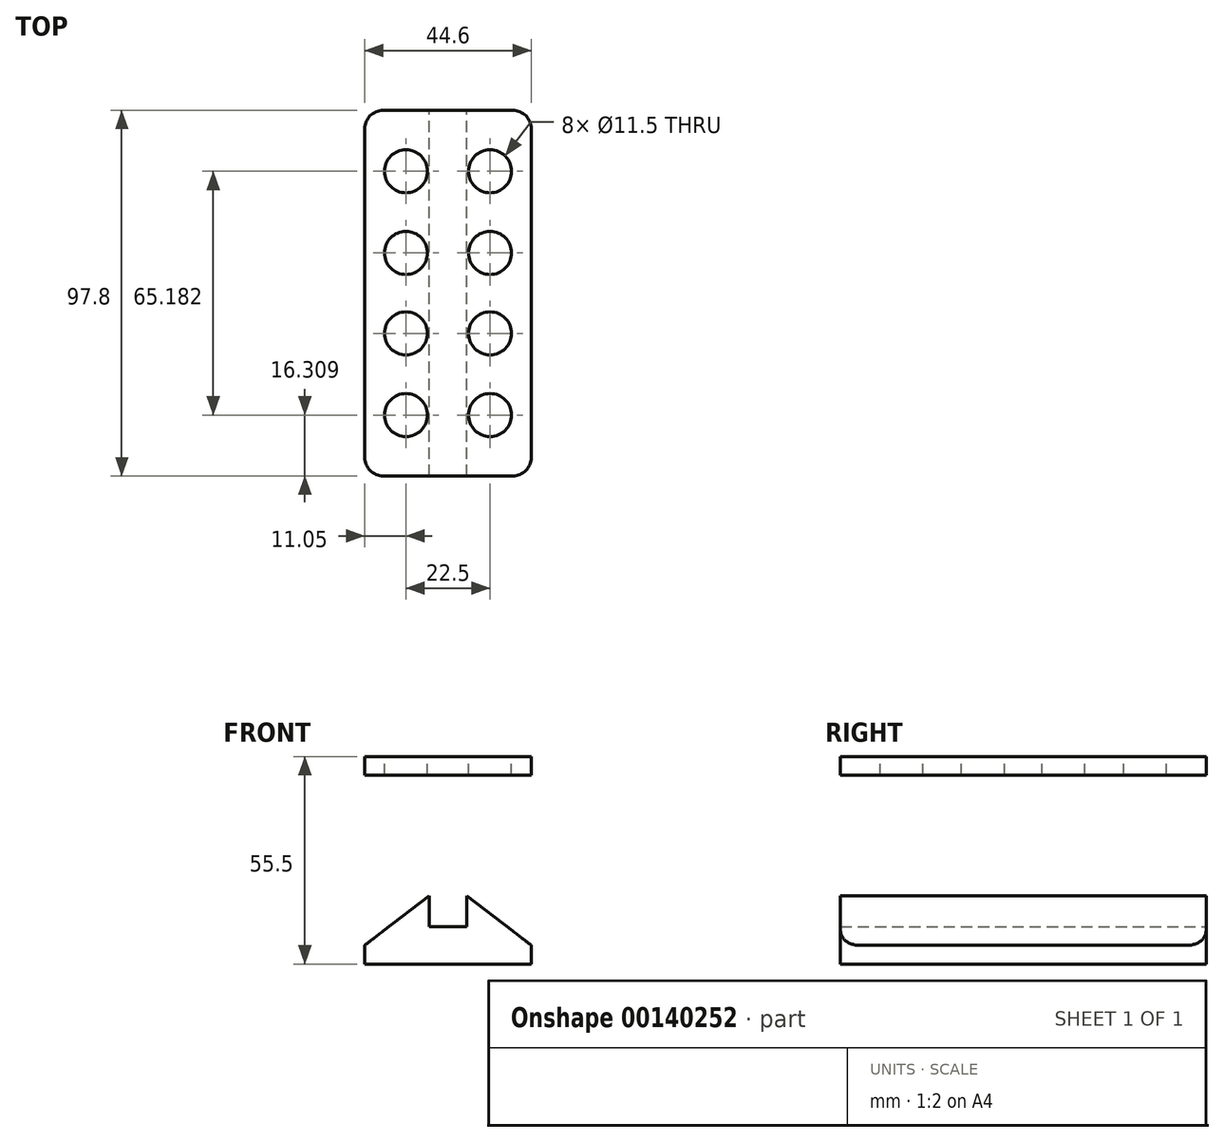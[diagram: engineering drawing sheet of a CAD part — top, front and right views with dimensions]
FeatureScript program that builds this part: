
annotation { "Feature Type Name" : "Feature", "Feature Type Description" : "" }
export const myFeature = defineFeature(function(context is Context, id is Id, definition is map)
    precondition{}
    {
        {
            var Q0;
            Q0=qCreatedBy(makeId("Front.planeOp"),FACE);
            var sketch = newSketch(context, id + "F0", { "sketchPlane" : qUnion([Q0])});
            skLineSegment(sketch, "E0.bottom", {"start": v(5, 20.25) * mm, "end": v(-5, 20.25) * mm});
            skLineSegment(sketch, "E0.top", {"start": v(5, -20.25) * mm, "end": v(-5, -20.25) * mm});
            skLineSegment(sketch, "E0.left", {"start": v(5, 20.25) * mm, "end": v(5, -20.25) * mm});
            skLineSegment(sketch, "E0.right", {"start": v(-5, 20.25) * mm, "end": v(-5, -20.25) * mm});
            skPoint(sketch, "E0.middle", {"position": v(0, 0) * mm});
            skLineSegment(sketch, "E1", {"start": v(-5, -20.25) * mm, "end": v(0, -20.25) * mm});
            skLineSegment(sketch, "E2", {"start": v(0, -20.25) * mm, "end": v(0, -22.75) * mm});
            skPoint(sketch, "E3.middle", {"position": v(0, -22.75) * mm});
            skLineSegment(sketch, "E4", {"start": v(5, 0) * mm, "end": v(5, -12) * mm});
            skLineSegment(sketch, "E5.MirrorCS", {"start": v(22.3, 20.25) * mm, "end": v(-22.3, 20.25) * mm});
            skLineSegment(sketch, "E6.MirrorCS", {"start": v(-22.3, 25.25) * mm, "end": v(-22.3, 20.25) * mm});
            skLineSegment(sketch, "E7.MirrorCS", {"start": v(22.3, 25.25) * mm, "end": v(-22.3, 25.25) * mm});
            skLineSegment(sketch, "E8.MirrorCS", {"start": v(22.3, 25.25) * mm, "end": v(22.3, 20.25) * mm});
            skLineSegment(sketch, "E9", {"start": v(-22.3, -25.25) * mm, "end": v(-22.3, -30.25) * mm});
            skLineSegment(sketch, "E10", {"start": v(22.3, -25.25) * mm, "end": v(22.3, -30.25) * mm});
            skLineSegment(sketch, "E11", {"start": v(22.3, -30.25) * mm, "end": v(-22.3, -30.25) * mm});
            skLineSegment(sketch, "E12", {"start": v(5, -12) * mm, "end": v(22.3, -25.25) * mm});
            skLineSegment(sketch, "E13.MirrorCS", {"start": v(-5, -12) * mm, "end": v(-22.3, -25.25) * mm});
            skSolve(sketch);
        }
        {
            var Q0;
            {var subQ3=sQuery(id+"F0.wireOp",EDGE,"UPzNgB99-kbm7-glpG-D5gg-bDxhdwpduCxz");Q0=makeQuery(id+"F0.imprint","IMPRINT",FACE,{"disambiguationData":[TD([[makeQuery(id+"F0.imprint","IMPRINT",EDGE,{"derivedFrom":subQ3}),-1.0]])]});}
            var Q1;
            Q1=makeQuery(id+"F0.imprint","IMPRINT",FACE,{"disambiguationData":[TD([[makeQuery(id+"F0.imprint","IMPRINT",EDGE,{"derivedFrom":sQuery(id+"F0.wireOp",EDGE,"E3.bottom")}),-1.0]])]});
            var Q2;
            {var subQ4=sQuery(id+"F0.wireOp",EDGE,"E6.MirrorCS");Q2=makeQuery(id+"F0.imprint","IMPRINT",FACE,{"disambiguationData":[TD([[makeQuery(id+"F0.imprint","IMPRINT",EDGE,{"derivedFrom":subQ4}),1.0]])]});}
            var Q3;
            {var subQ8=sQuery(id+"F0.wireOp",EDGE,"E4");Q3=makeQuery(id+"F0.imprint","IMPRINT",FACE,{"disambiguationData":[TD([[makeQuery(id+"F0.imprint","IMPRINT",EDGE,{"derivedFrom":subQ8}),-1.0]])]});}
            var Q4;
            {var subQ3=sQuery(id+"F0.wireOp",EDGE,"ce45a547-2342-4fc6-9943-eddce409deca0.MirrorCS");Q4=makeQuery(id+"F0.imprint","IMPRINT",FACE,{"disambiguationData":[TD([[makeQuery(id+"F0.imprint","IMPRINT",EDGE,{"derivedFrom":subQ3}),1.0]])]});}
            var Q5;
            {var subQ5=sQuery(id+"F0.wireOp",EDGE,"E0.top");Q5=makeQuery(id+"F0.imprint","IMPRINT",FACE,{"disambiguationData":[TD([[makeQuery(id+"F0.imprint","IMPRINT",EDGE,{"derivedFrom":subQ5}),1.0]])]});}
            extrude(context, id + "F1", {"entities" : qUnion([Q0, Q1, Q2, Q3, Q4, Q5]), "endBound" : BoundingType.SYMMETRIC, "depth" : 97.8 * mm});
        }
        {
            var Q0;
            Q0=makeQuery(id+"F1.opExtrude","CAP_EDGE",EDGE,{"disambiguationData":[OSD([sQuery(id+"F0.wireOp",EDGE,"E6.MirrorCS")])],"isStart":true});
            var Q1;
            Q1=makeQuery(id+"F1.opExtrude","CAP_EDGE",EDGE,{"disambiguationData":[OSD([sQuery(id+"F0.wireOp",EDGE,"E3.right")])],"isStart":true});
            var Q2;
            Q2=makeQuery(id+"F1.opExtrude","CAP_EDGE",EDGE,{"disambiguationData":[OSD([sQuery(id+"F0.wireOp",EDGE,"E3.right")])],"isStart":false});
            var Q3;
            Q3=makeQuery(id+"F1.opExtrude","CAP_EDGE",EDGE,{"disambiguationData":[OSD([sQuery(id+"F0.wireOp",EDGE,"E6.MirrorCS")])],"isStart":false});
            var Q4;
            Q4=makeQuery(id+"F1.opExtrude","CAP_EDGE",EDGE,{"disambiguationData":[OSD([sQuery(id+"F0.wireOp",EDGE,"E8.MirrorCS")])],"isStart":true});
            var Q5;
            Q5=makeQuery(id+"F1.opExtrude","CAP_EDGE",EDGE,{"disambiguationData":[OSD([sQuery(id+"F0.wireOp",EDGE,"E3.left")])],"isStart":true});
            var Q6;
            Q6=makeQuery(id+"F1.opExtrude","CAP_EDGE",EDGE,{"disambiguationData":[OSD([sQuery(id+"F0.wireOp",EDGE,"E8.MirrorCS")])],"isStart":false});
            var Q7;
            Q7=makeQuery(id+"F1.opExtrude","CAP_EDGE",EDGE,{"disambiguationData":[OSD([sQuery(id+"F0.wireOp",EDGE,"E3.left")])],"isStart":false});
            var Q8;
            Q8=makeQuery(id+"F1.opExtrude","CAP_EDGE",EDGE,{"disambiguationData":[OSD([sQuery(id+"F0.wireOp",EDGE,"E9")])],"isStart":false});
            var Q9;
            Q9=makeQuery(id+"F1.opExtrude","CAP_EDGE",EDGE,{"disambiguationData":[OSD([sQuery(id+"F0.wireOp",EDGE,"E10")])],"isStart":false});
            var Q10;
            Q10=makeQuery(id+"F1.opExtrude","CAP_EDGE",EDGE,{"disambiguationData":[OSD([sQuery(id+"F0.wireOp",EDGE,"E9")])],"isStart":true});
            var Q11;
            Q11=makeQuery(id+"F1.opExtrude","CAP_EDGE",EDGE,{"disambiguationData":[OSD([sQuery(id+"F0.wireOp",EDGE,"E10")])],"isStart":true});
            fillet(context, id + "F3", {"entities" : qUnion([Q0, Q1, Q2, Q3, Q4, Q5, Q6, Q7, Q8, Q9, Q10, Q11]), "radius" : 5 * mm, "tangentPropagation" : true, "allowEdgeOverflow" : false});
        }
        {
            var Q0;
            Q0=makeQuery(id+"F1.opExtrude","SWEPT_FACE",FACE,{"disambiguationData":[OSD([sQuery(id+"F0.wireOp",EDGE,"E0.right")])]});
            var sketch = newSketch(context, id + "F4", { "sketchPlane" : qUnion([Q0])});
            skLineSegment(sketch, "E14", {"start": v(0, 0) * mm, "end": v(10.8, 0) * mm});
            skLineSegment(sketch, "E15", {"start": v(10.8, 0) * mm, "end": v(32.4, 0) * mm});
            skLineSegment(sketch, "E16.MirrorCS", {"start": v(0, 0) * mm, "end": v(-10.8, 0) * mm});
            skLineSegment(sketch, "E17.MirrorCS", {"start": v(-10.8, 0) * mm, "end": v(-32.4, 0) * mm});
            skSolve(sketch);
        }
        {
            var Q0;
            Q0=sQuery(id+"F4.wireOp",VERTEX,"E15.end");
            var Q1;
            Q1=sQuery(id+"F4.wireOp",VERTEX,"E15.start");
            var Q2;
            Q2=sQuery(id+"F4.wireOp",VERTEX,"E17.MirrorCS.start");
            var Q3;
            Q3=sQuery(id+"F4.wireOp",VERTEX,"E17.MirrorCS.end");
            var Q4;
            Q4=makeQuery(id+"F1.opExtrude","SWEPT_BODY",BODY,{"disambiguationData":[OSD([sQuery(id+"F0.wireOp",EDGE,"E0.left"),sQuery(id+"F0.wireOp",EDGE,"E0.right"),sQuery(id+"F0.wireOp",EDGE,"E3.bottom"),sQuery(id+"F0.wireOp",EDGE,"E3.left"),sQuery(id+"F0.wireOp",EDGE,"E3.right"),sQuery(id+"F0.wireOp",EDGE,"E4"),sQuery(id+"F0.wireOp",EDGE,"UPzNgB99-kbm7-glpG-D5gg-bDxhdwpduCxz"),sQuery(id+"F0.wireOp",EDGE,"E6.MirrorCS"),sQuery(id+"F0.wireOp",EDGE,"E7.MirrorCS"),sQuery(id+"F0.wireOp",EDGE,"E8.MirrorCS"),sQuery(id+"F0.wireOp",EDGE,"E5.MirrorCS"),sQuery(id+"F0.wireOp",EDGE,"ce45a547-2342-4fc6-9943-eddce409deca0.MirrorCS")])]});
            hole(context, id + "F5", {"style" : HoleStyle.SIMPLE, "endStyle" : HoleEndStyle.THROUGH, "holeDiameter" : 11 * mm, "locations" : qUnion([Q0, Q1, Q2, Q3]), "scope" : qUnion([Q4]), "isTappedThrough" : true});
        }
        {
            var Q0;
            Q0=makeQuery(id+"F1.opExtrude","SWEPT_FACE",FACE,{"disambiguationData":[OSD([sQuery(id+"F0.wireOp",EDGE,"E7.MirrorCS")])]});
            var sketch = newSketch(context, id + "F6", { "sketchPlane" : qUnion([Q0])});
            skLineSegment(sketch, "E18", {"start": v(0, 32.6) * mm, "end": v(-11.25, 32.6) * mm});
            skLineSegment(sketch, "E19", {"start": v(0, 10.76) * mm, "end": v(-11.25, 10.76) * mm});
            skLineSegment(sketch, "E20.MirrorCS", {"start": v(0, 32.6) * mm, "end": v(11.25, 32.6) * mm});
            skLineSegment(sketch, "E21.MirrorCS", {"start": v(0, 10.76) * mm, "end": v(11.25, 10.76) * mm});
            skLineSegment(sketch, "E22.MirrorCS", {"start": v(0, -10.76) * mm, "end": v(11.25, -10.76) * mm});
            skLineSegment(sketch, "E23.MirrorCS", {"start": v(0, -10.76) * mm, "end": v(-11.25, -10.76) * mm});
            skLineSegment(sketch, "E24.MirrorCS", {"start": v(0, -32.6) * mm, "end": v(-11.25, -32.6) * mm});
            skLineSegment(sketch, "E25.MirrorCS", {"start": v(0, -32.6) * mm, "end": v(11.25, -32.6) * mm});
            skSolve(sketch);
        }
        {
            var Q0;
            Q0=sQuery(id+"F6.wireOp",VERTEX,"E18.end");
            var Q1;
            Q1=sQuery(id+"F6.wireOp",VERTEX,"E20.MirrorCS.end");
            var Q2;
            Q2=sQuery(id+"F6.wireOp",VERTEX,"E21.MirrorCS.end");
            var Q3;
            Q3=sQuery(id+"F6.wireOp",VERTEX,"E19.end");
            var Q4;
            Q4=sQuery(id+"F6.wireOp",VERTEX,"E23.MirrorCS.end");
            var Q5;
            Q5=sQuery(id+"F6.wireOp",VERTEX,"E22.MirrorCS.end");
            var Q6;
            Q6=sQuery(id+"F6.wireOp",VERTEX,"E25.MirrorCS.end");
            var Q7;
            Q7=sQuery(id+"F6.wireOp",VERTEX,"E24.MirrorCS.end");
            var Q8;
            Q8=makeQuery(id+"F1.opExtrude","SWEPT_BODY",BODY,{"disambiguationData":[OSD([sQuery(id+"F0.wireOp",EDGE,"E0.left"),sQuery(id+"F0.wireOp",EDGE,"E0.right"),sQuery(id+"F0.wireOp",EDGE,"E3.bottom"),sQuery(id+"F0.wireOp",EDGE,"E3.left"),sQuery(id+"F0.wireOp",EDGE,"E3.right"),sQuery(id+"F0.wireOp",EDGE,"E4"),sQuery(id+"F0.wireOp",EDGE,"UPzNgB99-kbm7-glpG-D5gg-bDxhdwpduCxz"),sQuery(id+"F0.wireOp",EDGE,"E6.MirrorCS"),sQuery(id+"F0.wireOp",EDGE,"E7.MirrorCS"),sQuery(id+"F0.wireOp",EDGE,"E8.MirrorCS"),sQuery(id+"F0.wireOp",EDGE,"E5.MirrorCS"),sQuery(id+"F0.wireOp",EDGE,"ce45a547-2342-4fc6-9943-eddce409deca0.MirrorCS")])]});
            hole(context, id + "F7", {"style" : HoleStyle.SIMPLE, "endStyle" : HoleEndStyle.BLIND, "holeDiameter" : 11.5 * mm, "holeDepth" : 12 * mm, "locations" : qUnion([Q0, Q1, Q2, Q3, Q4, Q5, Q6, Q7]), "scope" : qUnion([Q8])});
        }
    });
